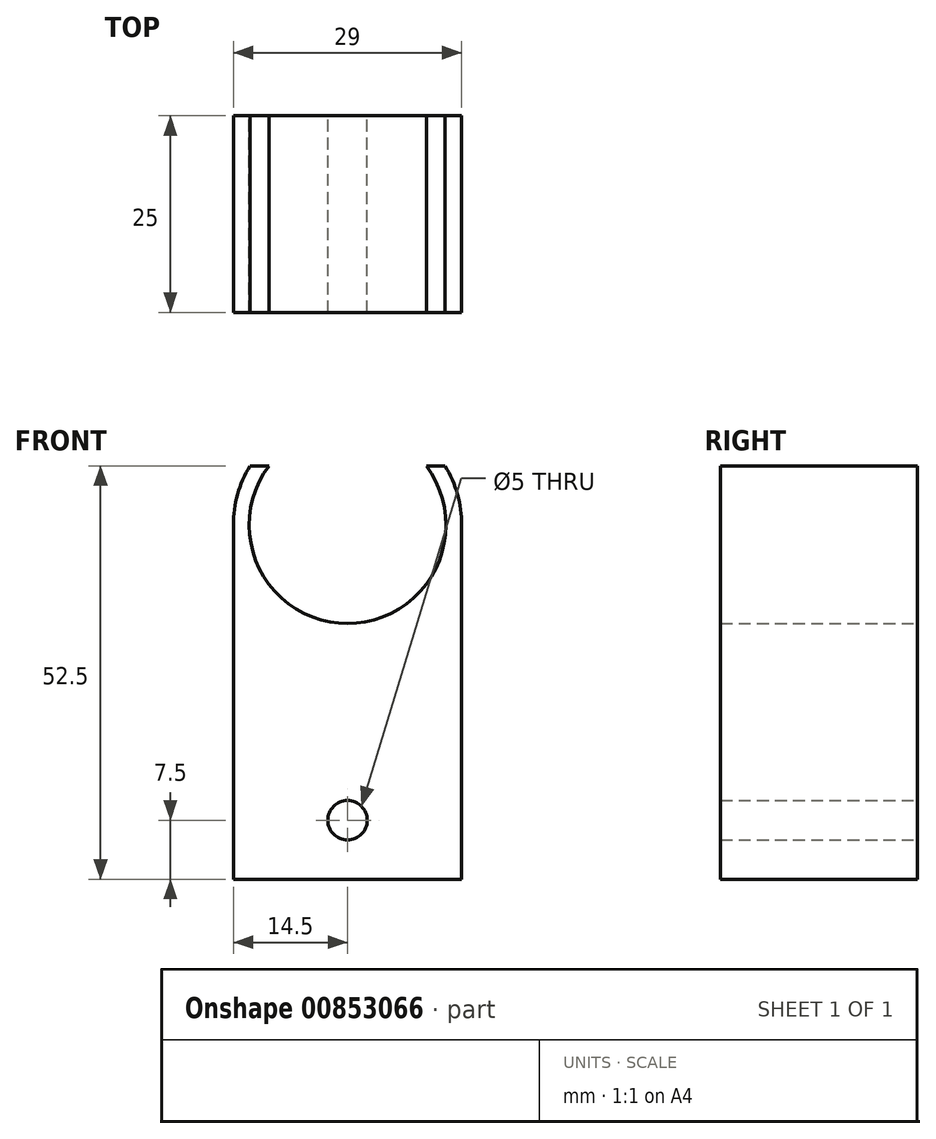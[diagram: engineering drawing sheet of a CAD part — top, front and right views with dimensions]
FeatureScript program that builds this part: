
annotation { "Feature Type Name" : "Feature", "Feature Type Description" : "" }
export const myFeature = defineFeature(function(context is Context, id is Id, definition is map)
    precondition{}
    {
        {
            var Q0;
            Q0=qCreatedBy(makeId("Front.planeOp"),FACE);
            var sketch = newSketch(context, id + "F0", { "sketchPlane" : qUnion([Q0])});
            skArc(sketch, "E0", {"start": v(-10, 7.5) * mm, "mid": v(0, -12.5) * mm, "end": v(10, 7.5) * mm});
            skArc(sketch, "E1", {"start": v(-12.4, 7.5) * mm, "mid": v(-13.97, 3.9) * mm, "end": v(-14.5, 0) * mm});
            skLineSegment(sketch, "E2", {"start": v(-14.5, 0) * mm, "end": v(-14.5, -45) * mm});
            skLineSegment(sketch, "E3", {"start": v(-14.5, -45) * mm, "end": v(14.5, -45) * mm});
            skLineSegment(sketch, "E4", {"start": v(14.5, -45) * mm, "end": v(14.5, 0) * mm});
            skLineSegment(sketch, "E5", {"start": v(-12.4, 7.5) * mm, "end": v(-10, 7.5) * mm});
            skLineSegment(sketch, "E6.trimOffspring", {"start": v(10, 7.5) * mm, "end": v(12.4, 7.5) * mm});
            skArc(sketch, "E7.trimOffspring", {"start": v(14.5, 0) * mm, "mid": v(13.97, 3.9) * mm, "end": v(12.4, 7.5) * mm});
            skCircle(sketch, "E8", {"center": v(0, -37.5) * mm, "radius": 2.5 * mm});
            skSolve(sketch);
        }
        {
            var Q0;
            Q0 = qSketchRegion(id + "F0", true);
            extrude(context, id + "F1", {"entities" : qUnion([Q0]), "depth" : 25 * mm, "offsetDistance" : 25 * mm});
        }
    });
